# Revit family: Food-Service-Equipment_Oscartek_Dgc30-46H_cat
name_source: partatom
category: Specialty Equipment
units: mm (PartAtom-declared; Revit-internal decimal feet)

## family parameters
Always vertical = Yes
Classification Number = 23.40.40.11.17
Cut with Voids When Loaded = No
Enable Cutting in Views = No
Maintain Annotation Orientation = No
Part Type = Normal
Room Calculation Point = No
Round Connector Dimension = Use Diameter
Shared = No
Work Plane-Based = No

## types (1)
- Food-Service-Equipment_Oscartek_Dgc30-46H_cat
    Apparent Power = 4775 VA
    Building Codes = https://www.arcat.com
    CSI Master Format = Refrigerated Food Storage Cases
    CSI MasterFormat = 11 41 13
    Conn Conduit = Yes
    Construction Details = http://www.oscartek.com
    Cycle = 60 Hz
    Default Elevation = 0"
    Depth = 44 1/4"
    Description = DIAMOND GELATO SHOWCASES
    FL Amps = 7 A
    Green Building-LEED = https://www.arcat.com
    Height = 46"
    Indirect Waste Connection Height = 0"
    Indirect Waste Size = 1"
    Installation-Fabrication = http://www.oscartek.com
    Length = 62"
    Light Length = 10"
    Manufacturer = OSCARTEK
    Manufacturer Fax = 650-342-7400
    Manufacturer Website = http://www.oscartek.com
    Max Overcurrent Protection = 0 A
    Min Ckt Ampacity = 0 A
    Model = DGC30-46H
    Phase = 3
    Product Data = http://www.oscartek.com
    Revision = R1_2018-10
    Sales Information = http://www.oscartek.com
    Specification = https://www.arcat.com
    Test Data = http://www.oscartek.com
    Type Comments = As Specified
    URL = www.oscartek.com
    URL Cutsheet = www.oscartek.com
    Volts = 400 V
    Watts = 2780 W
    Weight in Pounds = 650

## geometry (parser evidence)
native form markers: Blend x21, Sweep x8
no freeform markers — native parametric forms only
